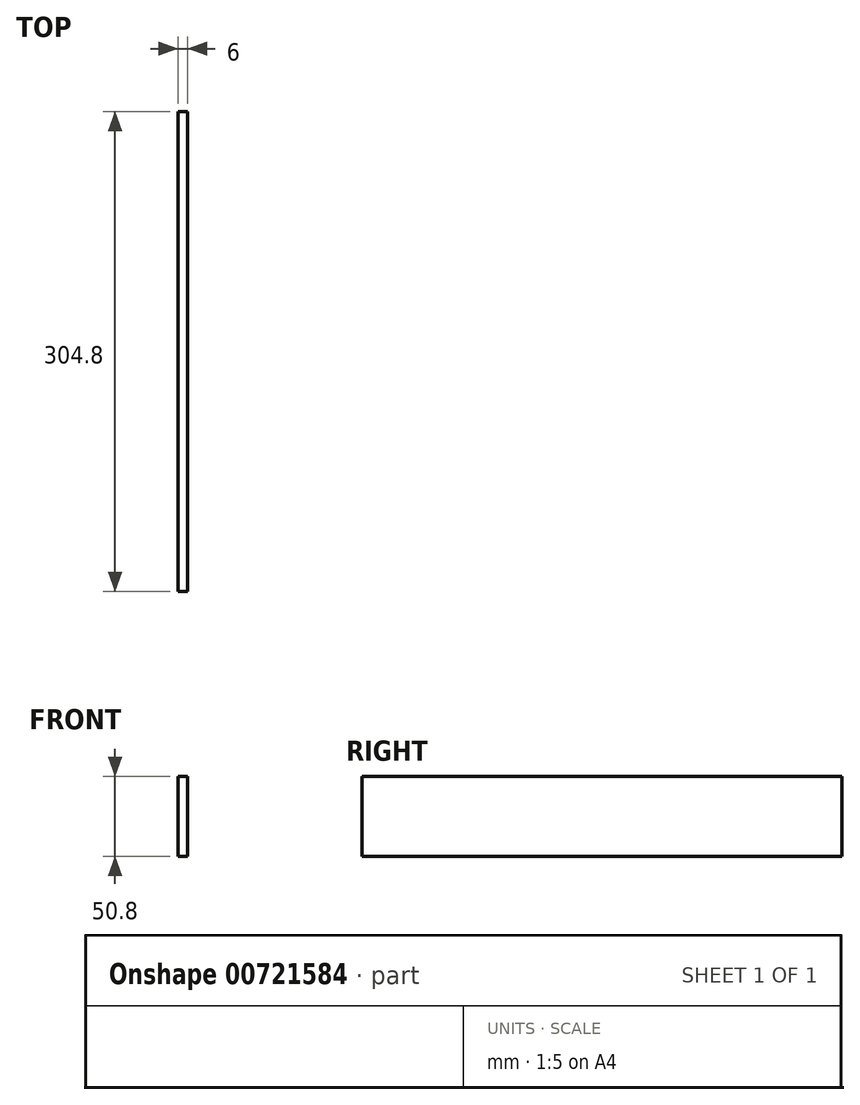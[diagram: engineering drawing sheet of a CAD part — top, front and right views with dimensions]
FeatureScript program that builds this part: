
annotation { "Feature Type Name" : "Feature", "Feature Type Description" : "" }
export const myFeature = defineFeature(function(context is Context, id is Id, definition is map)
    precondition{}
    {
        {
            var Q0;
            Q0=qCreatedBy(makeId("Right.planeOp"),FACE);
            var sketch = newSketch(context, id + "F0", { "sketchPlane" : qUnion([Q0])});
            skLineSegment(sketch, "E0.bottom", {"start": v(152.4, -25.4) * mm, "end": v(-152.4, -25.4) * mm});
            skLineSegment(sketch, "E0.top", {"start": v(152.4, 25.4) * mm, "end": v(-152.4, 25.4) * mm});
            skLineSegment(sketch, "E0.left", {"start": v(152.4, -25.4) * mm, "end": v(152.4, 25.4) * mm});
            skLineSegment(sketch, "E0.right", {"start": v(-152.4, -25.4) * mm, "end": v(-152.4, 25.4) * mm});
            skPoint(sketch, "E0.middle", {"position": v(0, 0) * mm});
            skSolve(sketch);
        }
        {
            var Q0;
            Q0 = qSketchRegion(id + "F0", true);
            extrude(context, id + "F1", {"entities" : qUnion([Q0]), "depth" : 6 * mm, "offsetDistance" : 25.4 * mm, "symmetric" : true});
        }
    });
